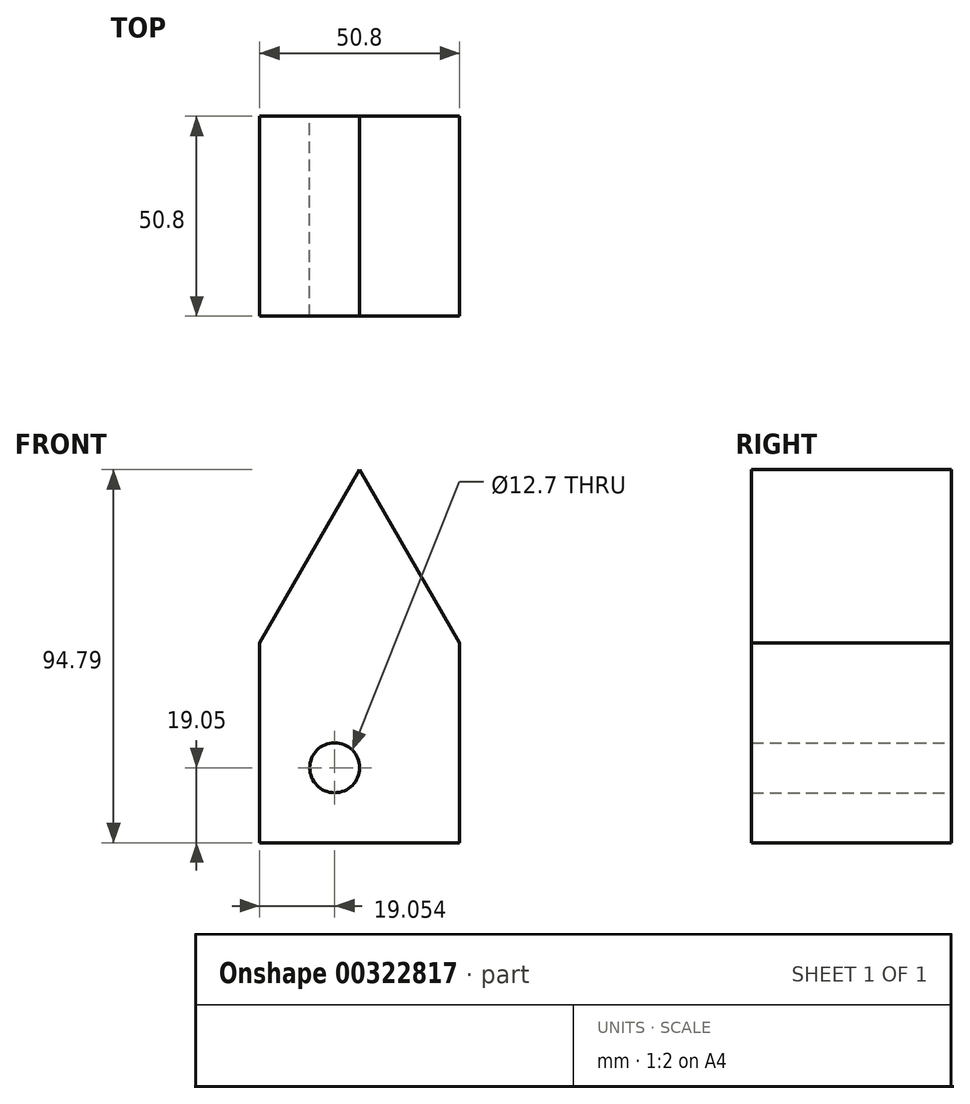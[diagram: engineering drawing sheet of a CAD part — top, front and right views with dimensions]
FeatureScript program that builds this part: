
annotation { "Feature Type Name" : "Feature", "Feature Type Description" : "" }
export const myFeature = defineFeature(function(context is Context, id is Id, definition is map)
    precondition{}
    {
        {
            var Q0;
            Q0=qCreatedBy(makeId("Front.planeOp"),FACE);
            var sketch = newSketch(context, id + "F0", { "sketchPlane" : qUnion([Q0])});
            skLineSegment(sketch, "E0.top", {"start": v(-62, 0) * mm, "end": v(-11.2, 0) * mm});
            skLineSegment(sketch, "E0.left", {"start": v(-62, 50.8) * mm, "end": v(-62, 0) * mm});
            skLineSegment(sketch, "E0.right", {"start": v(-11.2, 50.8) * mm, "end": v(-11.2, 0) * mm});
            skLineSegment(sketch, "E1", {"start": v(-62, 50.8) * mm, "end": v(-36.6, 94.8) * mm});
            skLineSegment(sketch, "E2", {"start": v(-11.2, 50.8) * mm, "end": v(-36.6, 94.8) * mm});
            skCircle(sketch, "E3", {"center": v(-42.95, 19.05) * mm, "radius": 6.35 * mm});
            skSolve(sketch);
        }
        {
            var Q0;
            Q0 = qSketchRegion(id + "F0", true);
            extrude(context, id + "F1", {"entities" : qUnion([Q0]), "depth" : 50.8 * mm});
        }
    });
